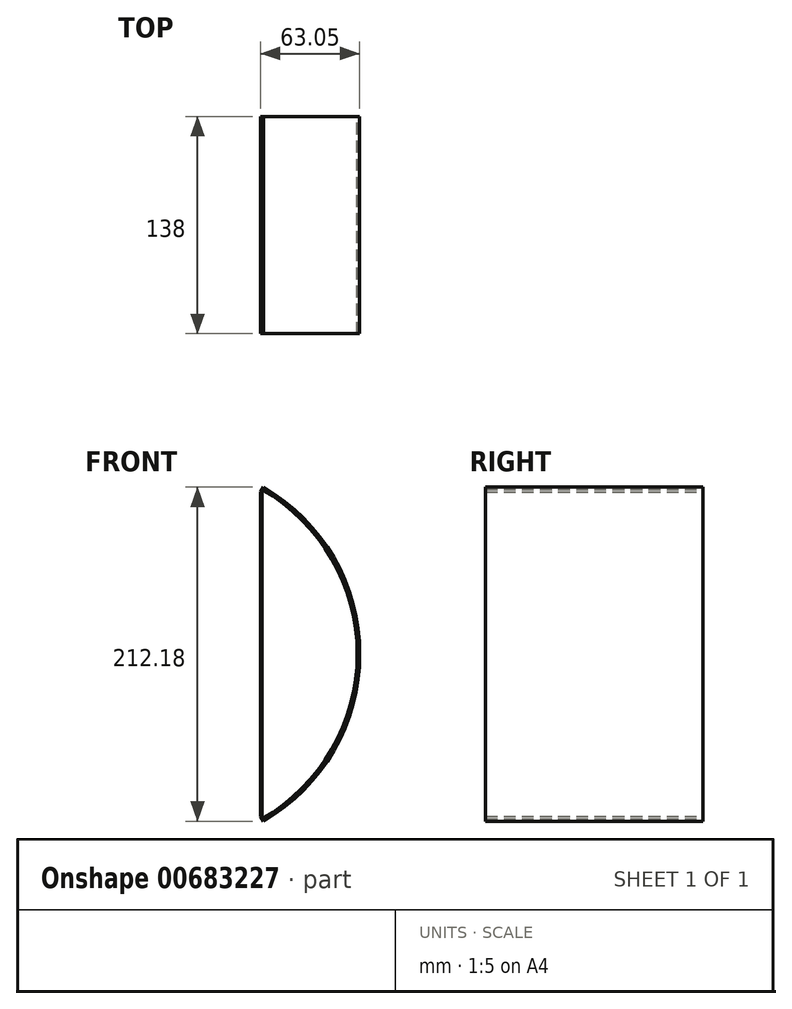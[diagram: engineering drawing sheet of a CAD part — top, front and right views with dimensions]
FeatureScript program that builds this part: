
annotation { "Feature Type Name" : "Feature", "Feature Type Description" : "" }
export const myFeature = defineFeature(function(context is Context, id is Id, definition is map)
    precondition{}
    {
        {
            var Q0;
            Q0=qCreatedBy(makeId("Front.planeOp"),FACE);
            var sketch = newSketch(context, id + "F0", { "sketchPlane" : qUnion([Q0])});
            skLineSegment(sketch, "E0", {"start": v(0, 0) * mm, "end": v(0, -238.35) * mm});
            skArc(sketch, "E1", {"start": v(60.45, -104.7) * mm, "mid": v(120.9, 0) * mm, "end": v(60.45, 104.7) * mm});
            skLineSegment(sketch, "E2", {"start": v(0, 0) * mm, "end": v(0, 205.65) * mm});
            skLineSegment(sketch, "E3", {"start": v(0, 0) * mm, "end": v(121.78, 210.93) * mm});
            skLineSegment(sketch, "E4", {"start": v(0, 0) * mm, "end": v(101.02, -174.98) * mm});
            skArc(sketch, "E5.0", {"start": v(61.25, -106.09) * mm, "mid": v(122.5, 0) * mm, "end": v(61.25, 106.09) * mm});
            skLineSegment(sketch, "E6", {"start": v(60.45, 104.7) * mm, "end": v(60.45, -104.7) * mm});
            skLineSegment(sketch, "E7.0", {"start": v(59.45, 104.7) * mm, "end": v(59.45, -104.7) * mm});
            skSolve(sketch);
        }
        {
            var Q0;
            {var subQ0=sQuery(id+"F0.wireOp",EDGE,"E1");Q0=makeQuery(id+"F0.imprint","IMPRINT",FACE,{"disambiguationData":[TD([[makeQuery(id+"F0.imprint","IMPRINT",EDGE,{"derivedFrom":subQ0}),-1.0]])]});}
            var Q1;
            {var subQ0=sQuery(id+"F0.wireOp",EDGE,"E6");Q1=makeQuery(id+"F0.imprint","IMPRINT",FACE,{"disambiguationData":[TD([[makeQuery(id+"F0.imprint","IMPRINT",EDGE,{"derivedFrom":subQ0}),-1.0]])]});}
            extrude(context, id + "F1", {"entities" : qUnion([Q0, Q1]), "depth" : 138 * mm, "offsetDistance" : 25 * mm});
        }
    });
